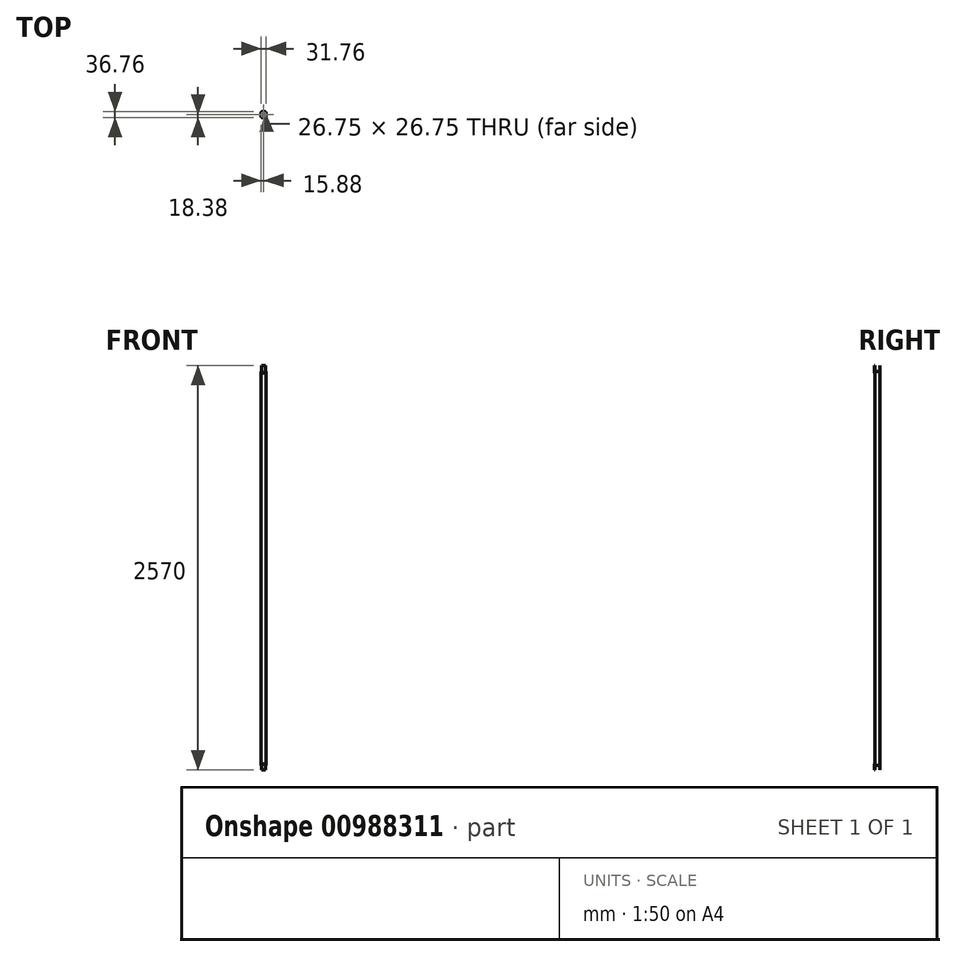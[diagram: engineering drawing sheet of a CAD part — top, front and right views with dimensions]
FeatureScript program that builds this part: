
annotation { "Feature Type Name" : "Feature", "Feature Type Description" : "" }
export const myFeature = defineFeature(function(context is Context, id is Id, definition is map)
    precondition{}
    {
        {
            var Q0;
            Q0=qCreatedBy(makeId("Top.planeOp"),FACE);
            var sketch = newSketch(context, id + "F0", { "sketchPlane" : qUnion([Q0])});
            skLineSegment(sketch, "E0.bottom", {"start": v(13.38, 15.88) * mm, "end": v(-13.38, 15.88) * mm});
            skLineSegment(sketch, "E0.top", {"start": v(13.37, -15.88) * mm, "end": v(-13.37, -15.88) * mm});
            skLineSegment(sketch, "E0.left", {"start": v(15.88, 13.38) * mm, "end": v(15.88, -13.37) * mm});
            skLineSegment(sketch, "E0.right", {"start": v(-15.88, 13.38) * mm, "end": v(-15.88, -13.37) * mm});
            skPoint(sketch, "E0.middle", {"position": v(0, 0) * mm});
            skPoint(sketch, "E1.visualSharp", {"position": v(-15.88, 15.88) * mm});
            skArc(sketch, "E1.filletArc", {"start": v(-13.38, 15.88) * mm, "mid": v(-15.14, 15.14) * mm, "end": v(-15.88, 13.38) * mm});
            skPoint(sketch, "E2.visualSharp", {"position": v(15.88, 15.88) * mm});
            skArc(sketch, "E2.filletArc", {"start": v(15.88, 13.38) * mm, "mid": v(15.14, 15.14) * mm, "end": v(13.38, 15.88) * mm});
            skPoint(sketch, "E3.visualSharp", {"position": v(15.88, -15.88) * mm});
            skArc(sketch, "E3.filletArc", {"start": v(13.37, -15.88) * mm, "mid": v(15.14, -15.14) * mm, "end": v(15.88, -13.37) * mm});
            skPoint(sketch, "E4.visualSharp", {"position": v(-15.88, -15.88) * mm});
            skArc(sketch, "E4.filletArc", {"start": v(-15.88, -13.37) * mm, "mid": v(-15.14, -15.14) * mm, "end": v(-13.37, -15.88) * mm});
            skLineSegment(sketch, "E5.0", {"start": v(13.38, 13.38) * mm, "end": v(13.38, 13.38) * mm});
            skLineSegment(sketch, "E5.1", {"start": v(13.38, 13.38) * mm, "end": v(13.38, -13.38) * mm});
            skLineSegment(sketch, "E5.2", {"start": v(13.38, 13.38) * mm, "end": v(-13.37, 13.38) * mm});
            skLineSegment(sketch, "E5.3", {"start": v(13.37, -13.37) * mm, "end": v(13.37, -13.37) * mm});
            skLineSegment(sketch, "E5.4", {"start": v(-13.37, 13.37) * mm, "end": v(-13.37, 13.37) * mm});
            skLineSegment(sketch, "E5.5", {"start": v(-13.37, 13.38) * mm, "end": v(-13.37, -13.38) * mm});
            skLineSegment(sketch, "E5.6", {"start": v(-13.37, -13.37) * mm, "end": v(-13.37, -13.37) * mm});
            skLineSegment(sketch, "E5.7", {"start": v(13.38, -13.38) * mm, "end": v(-13.37, -13.38) * mm});
            skSolve(sketch);
        }
        {
            var Q0;
            Q0=makeQuery(id+"F0.imprint","IMPRINT",FACE,{"disambiguationData":[TD([[makeQuery(id+"F0.imprint","IMPRINT",EDGE,{"derivedFrom":sQuery(id+"F0.wireOp",EDGE,"E0.bottom")}),1.0]])]});
            extrude(context, id + "F1", {"entities" : qUnion([Q0]), "depth" : 2500 * mm, "offsetDistance" : 25 * mm});
        }
        {
            var Q0;
            Q0=makeQuery(id+"F1.opExtrude","SWEPT_FACE",FACE,{"disambiguationData":[OSD([sQuery(id+"F0.wireOp",EDGE,"E0.top")])]});
            var sketch = newSketch(context, id + "F2", { "sketchPlane" : qUnion([Q0])});
            skLineSegment(sketch, "E6.bottom", {"start": v(-13.37, 2490) * mm, "end": v(13.37, 2490) * mm});
            skLineSegment(sketch, "E6.top", {"start": v(-13.38, 2540) * mm, "end": v(13.37, 2540) * mm});
            skLineSegment(sketch, "E6.left", {"start": v(-13.37, 2490) * mm, "end": v(-13.37, 2540) * mm});
            skLineSegment(sketch, "E6.right", {"start": v(13.37, 2490) * mm, "end": v(13.37, 2540) * mm});
            skLineSegment(sketch, "E7.bottom", {"start": v(-13.37, 10) * mm, "end": v(13.37, 10) * mm});
            skLineSegment(sketch, "E7.top", {"start": v(-13.37, -30) * mm, "end": v(13.37, -30) * mm});
            skLineSegment(sketch, "E7.left", {"start": v(-13.37, 10) * mm, "end": v(-13.37, -30) * mm});
            skLineSegment(sketch, "E7.right", {"start": v(13.37, 10) * mm, "end": v(13.37, -30) * mm});
            skSolve(sketch);
        }
        {
            var Q0;
            Q0 = qSketchRegion(id + "F2", true);
            extrude(context, id + "F3", {"entities" : qUnion([Q0]), "depth" : 2.5 * mm, "offsetDistance" : 25 * mm});
        }
        {
            var Q0;
            Q0=makeQuery(id+"F3.opExtrude","SWEPT_BODY",BODY,{"disambiguationData":[OSD([sQuery(id+"F2.wireOp",EDGE,"E6.bottom"),sQuery(id+"F2.wireOp",EDGE,"E6.top"),sQuery(id+"F2.wireOp",EDGE,"E6.left"),sQuery(id+"F2.wireOp",EDGE,"E6.right")])]});
            var Q1;
            Q1=makeQuery(id+"F3.opExtrude","SWEPT_BODY",BODY,{"disambiguationData":[OSD([sQuery(id+"F2.wireOp",EDGE,"E7.bottom"),sQuery(id+"F2.wireOp",EDGE,"E7.top"),sQuery(id+"F2.wireOp",EDGE,"E7.left"),sQuery(id+"F2.wireOp",EDGE,"E7.right")])]});
            var Q2;
            Q2=qCreatedBy(makeId("Front.planeOp"),FACE);
            mirror(context, id + "F4", {"operationType" : NewBodyOperationType.ADD, "entities" : qUnion([Q0, Q1]), "mirrorPlane" : qUnion([Q2])});
        }
    });
